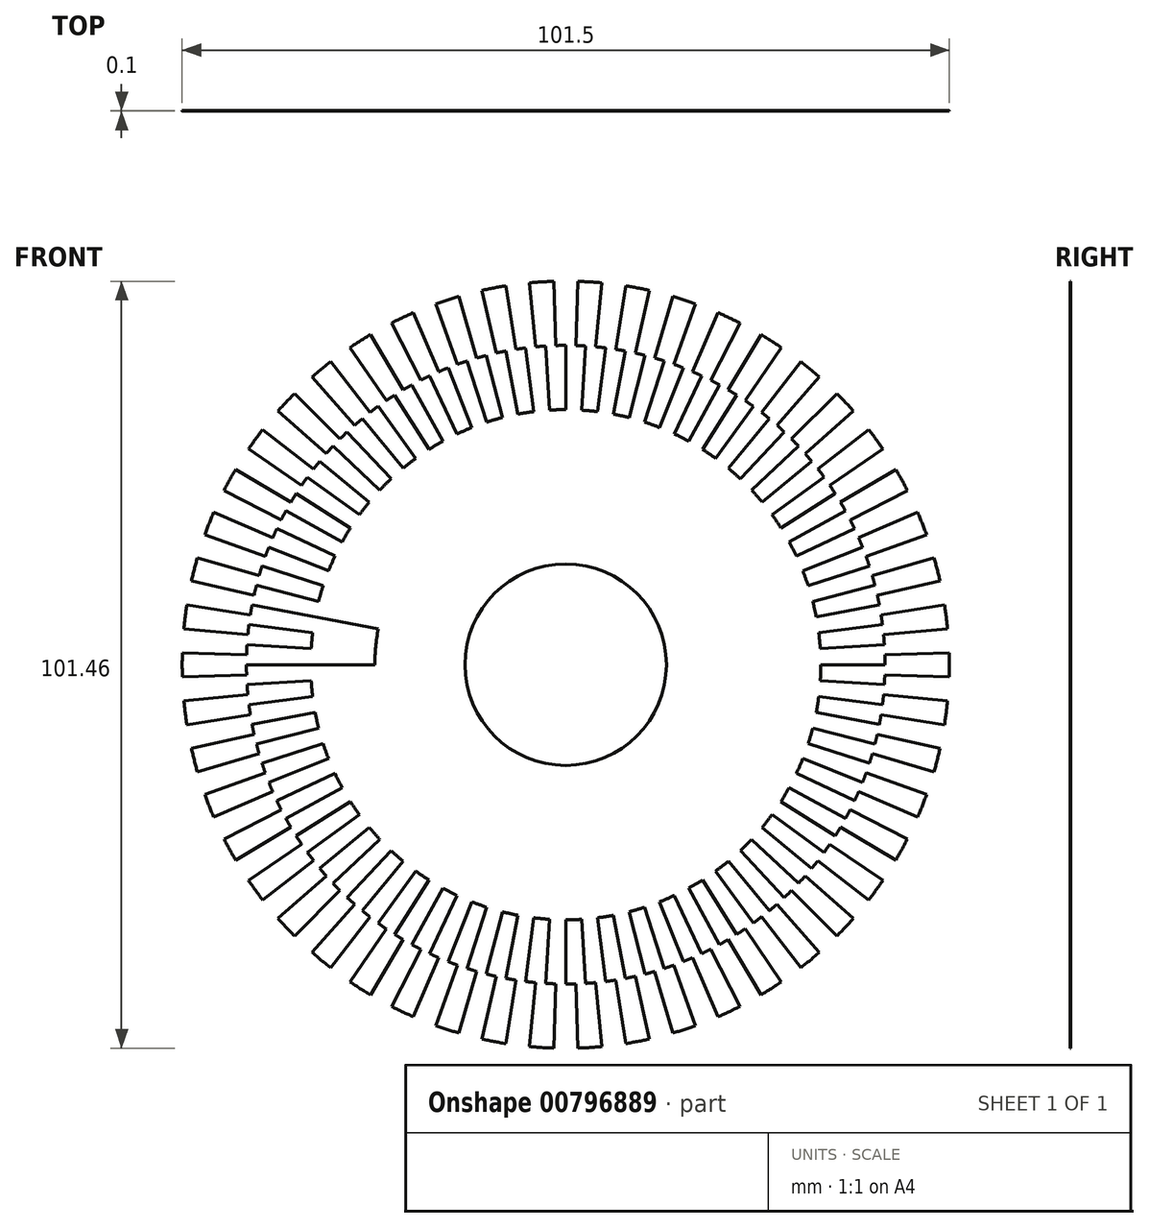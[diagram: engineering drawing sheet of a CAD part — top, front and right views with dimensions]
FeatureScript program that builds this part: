
annotation { "Feature Type Name" : "Feature", "Feature Type Description" : "" }
export const myFeature = defineFeature(function(context is Context, id is Id, definition is map)
    precondition{}
    {
        {
            var Q0;
            Q0=qCreatedBy(makeId("Front.planeOp"),FACE);
            var sketch = newSketch(context, id + "F0", { "sketchPlane" : qUnion([Q0])});
            skCircle(sketch, "E0", {"center": v(0, 0) * mm, "radius": 38 * mm, "construction": true});
            skCircle(sketch, "E1", {"center": v(0, 0) * mm, "radius": 29.5 * mm, "construction": true});
            skCircle(sketch, "E2", {"center": v(0, 0) * mm, "radius": 46.5 * mm, "construction": true});
            skArc(sketch, "E3.0", {"start": v(-33.68, 2.12) * mm, "mid": v(-33.73, 1.06) * mm, "end": v(-33.75, 0) * mm});
            skArc(sketch, "E4.0", {"start": v(-42.17, 2.65) * mm, "mid": v(-42.25, 0.66) * mm, "end": v(-42.23, -1.33) * mm});
            skArc(sketch, "E5.0", {"start": v(-50.73, 1.6) * mm, "mid": v(-50.75, 0) * mm, "end": v(-50.73, -1.6) * mm});
            skLineSegment(sketch, "E6", {"start": v(-25.25, 0) * mm, "end": v(-33.75, 0) * mm});
            skLineSegment(sketch, "E7.trimOffspring", {"start": v(-33.68, 2.12) * mm, "end": v(-42.17, 2.65) * mm});
            skLineSegment(sketch, "E8.trimOffspring", {"start": v(-33.75, 0) * mm, "end": v(-42.25, 0) * mm});
            skLineSegment(sketch, "E9.trimOffspring", {"start": v(-42.23, 1.33) * mm, "end": v(-50.73, 1.6) * mm});
            skLineSegment(sketch, "E10.trimOffspring", {"start": v(-42.23, -1.33) * mm, "end": v(-50.73, -1.6) * mm});
            skLineSegment(sketch, "E11", {"start": v(-24.8, 4.73) * mm, "end": v(-33.15, 6.32) * mm});
            skArc(sketch, "E12", {"start": v(-25.25, 0) * mm, "mid": v(-25.14, 2.38) * mm, "end": v(-24.8, 4.73) * mm});
            skArc(sketch, "E13", {"start": v(-33.75, 0) * mm, "mid": v(-33.6, 3.18) * mm, "end": v(-33.15, 6.32) * mm});
            skLineSegment(sketch, "E14", {"start": v(0, 0) * mm, "end": v(-70.43, 0) * mm, "construction": true});
            skLineSegment(sketch, "E15", {"start": v(0, 0) * mm, "end": v(-33.68, 2.12) * mm, "construction": true});
            skLineSegment(sketch, "E16", {"start": v(0, 0) * mm, "end": v(-42.23, -1.33) * mm, "construction": true});
            skLineSegment(sketch, "E17", {"start": v(0, 0) * mm, "end": v(-42.23, 1.33) * mm, "construction": true});
            skLineSegment(sketch, "E18.1.0", {"start": v(-41.73, -6.6) * mm, "end": v(-50.13, -7.94) * mm});
            skArc(sketch, "E18.1.1", {"start": v(-50.53, -4.78) * mm, "mid": v(-50.35, -6.36) * mm, "end": v(-50.13, -7.94) * mm});
            skLineSegment(sketch, "E18.1.2", {"start": v(-42.06, -3.98) * mm, "end": v(-50.53, -4.78) * mm});
            skArc(sketch, "E18.1.3", {"start": v(-42.17, -2.65) * mm, "mid": v(-42, -4.64) * mm, "end": v(-41.73, -6.6) * mm});
            skLineSegment(sketch, "E18.1.4", {"start": v(-33.68, -2.12) * mm, "end": v(-42.17, -2.65) * mm});
            skArc(sketch, "E18.1.5", {"start": v(-33.68, -2.12) * mm, "mid": v(-33.6, -3.18) * mm, "end": v(-33.48, -4.23) * mm});
            skLineSegment(sketch, "E18.1.6", {"start": v(-33.48, -4.23) * mm, "end": v(-41.92, -5.3) * mm});
            skLineSegment(sketch, "E18.2.0", {"start": v(-40.57, -11.79) * mm, "end": v(-48.74, -14.16) * mm});
            skArc(sketch, "E18.2.1", {"start": v(-49.53, -11.07) * mm, "mid": v(-49.16, -12.62) * mm, "end": v(-48.74, -14.16) * mm});
            skLineSegment(sketch, "E18.2.2", {"start": v(-41.23, -9.22) * mm, "end": v(-49.53, -11.07) * mm});
            skArc(sketch, "E18.2.3", {"start": v(-41.5, -7.92) * mm, "mid": v(-41.08, -9.86) * mm, "end": v(-40.57, -11.79) * mm});
            skLineSegment(sketch, "E18.2.4", {"start": v(-33.15, -6.32) * mm, "end": v(-41.5, -7.92) * mm});
            skArc(sketch, "E18.2.5", {"start": v(-33.15, -6.32) * mm, "mid": v(-32.94, -7.36) * mm, "end": v(-32.7, -8.4) * mm});
            skLineSegment(sketch, "E18.2.6", {"start": v(-32.7, -8.4) * mm, "end": v(-40.92, -10.5) * mm});
            skLineSegment(sketch, "E18.3.0", {"start": v(-38.78, -16.78) * mm, "end": v(-46.58, -20.16) * mm});
            skArc(sketch, "E18.3.1", {"start": v(-47.75, -17.2) * mm, "mid": v(-47.19, -18.68) * mm, "end": v(-46.58, -20.16) * mm});
            skLineSegment(sketch, "E18.3.2", {"start": v(-39.75, -14.31) * mm, "end": v(-47.75, -17.2) * mm});
            skArc(sketch, "E18.3.3", {"start": v(-40.18, -13.06) * mm, "mid": v(-39.52, -14.93) * mm, "end": v(-38.78, -16.78) * mm});
            skLineSegment(sketch, "E18.3.4", {"start": v(-32.1, -10.43) * mm, "end": v(-40.18, -13.06) * mm});
            skArc(sketch, "E18.3.5", {"start": v(-32.1, -10.43) * mm, "mid": v(-31.76, -11.43) * mm, "end": v(-31.38, -12.42) * mm});
            skLineSegment(sketch, "E18.3.6", {"start": v(-31.38, -12.42) * mm, "end": v(-39.28, -15.55) * mm});
            skLineSegment(sketch, "E18.4.0", {"start": v(-36.37, -21.5) * mm, "end": v(-43.68, -25.83) * mm});
            skArc(sketch, "E18.4.1", {"start": v(-45.22, -23.04) * mm, "mid": v(-44.47, -24.45) * mm, "end": v(-43.68, -25.83) * mm});
            skLineSegment(sketch, "E18.4.2", {"start": v(-37.65, -19.18) * mm, "end": v(-45.22, -23.04) * mm});
            skArc(sketch, "E18.4.3", {"start": v(-38.23, -17.99) * mm, "mid": v(-37.34, -19.77) * mm, "end": v(-36.37, -21.5) * mm});
            skLineSegment(sketch, "E18.4.4", {"start": v(-30.54, -14.37) * mm, "end": v(-38.23, -17.99) * mm});
            skArc(sketch, "E18.4.5", {"start": v(-30.54, -14.37) * mm, "mid": v(-30.07, -15.32) * mm, "end": v(-29.58, -16.26) * mm});
            skLineSegment(sketch, "E18.4.6", {"start": v(-29.58, -16.26) * mm, "end": v(-37.02, -20.35) * mm});
            skLineSegment(sketch, "E18.5.0", {"start": v(-33.38, -25.9) * mm, "end": v(-40.1, -31.1) * mm});
            skArc(sketch, "E18.5.1", {"start": v(-41.98, -28.53) * mm, "mid": v(-41.06, -29.83) * mm, "end": v(-40.1, -31.1) * mm});
            skLineSegment(sketch, "E18.5.2", {"start": v(-34.94, -23.75) * mm, "end": v(-41.98, -28.53) * mm});
            skArc(sketch, "E18.5.3", {"start": v(-35.67, -22.64) * mm, "mid": v(-34.57, -24.3) * mm, "end": v(-33.38, -25.9) * mm});
            skLineSegment(sketch, "E18.5.4", {"start": v(-28.5, -18.08) * mm, "end": v(-35.67, -22.64) * mm});
            skArc(sketch, "E18.5.5", {"start": v(-28.5, -18.08) * mm, "mid": v(-27.91, -18.97) * mm, "end": v(-27.3, -19.84) * mm});
            skLineSegment(sketch, "E18.5.6", {"start": v(-27.3, -19.84) * mm, "end": v(-34.18, -24.83) * mm});
            skLineSegment(sketch, "E18.6.0", {"start": v(-29.88, -29.88) * mm, "end": v(-35.89, -35.89) * mm});
            skArc(sketch, "E18.6.1", {"start": v(-38.07, -33.56) * mm, "mid": v(-37, -34.74) * mm, "end": v(-35.89, -35.89) * mm});
            skLineSegment(sketch, "E18.6.2", {"start": v(-31.7, -27.94) * mm, "end": v(-38.07, -33.56) * mm});
            skArc(sketch, "E18.6.3", {"start": v(-32.55, -26.93) * mm, "mid": v(-31.25, -28.44) * mm, "end": v(-29.88, -29.88) * mm});
            skLineSegment(sketch, "E18.6.4", {"start": v(-26, -21.51) * mm, "end": v(-32.55, -26.93) * mm});
            skArc(sketch, "E18.6.5", {"start": v(-26, -21.51) * mm, "mid": v(-25.32, -22.32) * mm, "end": v(-24.6, -23.1) * mm});
            skLineSegment(sketch, "E18.6.6", {"start": v(-24.6, -23.1) * mm, "end": v(-30.8, -28.92) * mm});
            skLineSegment(sketch, "E18.7.0", {"start": v(-25.9, -33.38) * mm, "end": v(-31.1, -40.1) * mm});
            skArc(sketch, "E18.7.1", {"start": v(-33.56, -38.07) * mm, "mid": v(-32.35, -39.1) * mm, "end": v(-31.1, -40.1) * mm});
            skLineSegment(sketch, "E18.7.2", {"start": v(-27.94, -31.7) * mm, "end": v(-33.56, -38.07) * mm});
            skArc(sketch, "E18.7.3", {"start": v(-28.92, -30.8) * mm, "mid": v(-27.44, -32.13) * mm, "end": v(-25.9, -33.38) * mm});
            skLineSegment(sketch, "E18.7.4", {"start": v(-23.1, -24.6) * mm, "end": v(-28.92, -30.8) * mm});
            skArc(sketch, "E18.7.5", {"start": v(-23.1, -24.6) * mm, "mid": v(-22.32, -25.32) * mm, "end": v(-21.51, -26) * mm});
            skLineSegment(sketch, "E18.7.6", {"start": v(-21.51, -26) * mm, "end": v(-26.93, -32.55) * mm});
            skLineSegment(sketch, "E18.8.0", {"start": v(-21.5, -36.37) * mm, "end": v(-25.83, -43.68) * mm});
            skArc(sketch, "E18.8.1", {"start": v(-28.53, -41.98) * mm, "mid": v(-27.2, -42.85) * mm, "end": v(-25.83, -43.68) * mm});
            skLineSegment(sketch, "E18.8.2", {"start": v(-23.75, -34.94) * mm, "end": v(-28.53, -41.98) * mm});
            skArc(sketch, "E18.8.3", {"start": v(-24.83, -34.18) * mm, "mid": v(-23.2, -35.31) * mm, "end": v(-21.5, -36.37) * mm});
            skLineSegment(sketch, "E18.8.4", {"start": v(-19.84, -27.3) * mm, "end": v(-24.83, -34.18) * mm});
            skArc(sketch, "E18.8.5", {"start": v(-19.84, -27.3) * mm, "mid": v(-18.97, -27.91) * mm, "end": v(-18.08, -28.5) * mm});
            skLineSegment(sketch, "E18.8.6", {"start": v(-18.08, -28.5) * mm, "end": v(-22.64, -35.67) * mm});
            skLineSegment(sketch, "E18.9.0", {"start": v(-16.78, -38.78) * mm, "end": v(-20.16, -46.58) * mm});
            skArc(sketch, "E18.9.1", {"start": v(-23.04, -45.22) * mm, "mid": v(-21.6, -45.92) * mm, "end": v(-20.16, -46.58) * mm});
            skLineSegment(sketch, "E18.9.2", {"start": v(-19.18, -37.65) * mm, "end": v(-23.04, -45.22) * mm});
            skArc(sketch, "E18.9.3", {"start": v(-20.35, -37.02) * mm, "mid": v(-18.59, -37.94) * mm, "end": v(-16.78, -38.78) * mm});
            skLineSegment(sketch, "E18.9.4", {"start": v(-16.26, -29.58) * mm, "end": v(-20.35, -37.02) * mm});
            skArc(sketch, "E18.9.5", {"start": v(-16.26, -29.58) * mm, "mid": v(-15.32, -30.07) * mm, "end": v(-14.37, -30.54) * mm});
            skLineSegment(sketch, "E18.9.6", {"start": v(-14.37, -30.54) * mm, "end": v(-17.99, -38.23) * mm});
            skLineSegment(sketch, "E18.10.0", {"start": v(-11.79, -40.57) * mm, "end": v(-14.16, -48.74) * mm});
            skArc(sketch, "E18.10.1", {"start": v(-17.2, -47.75) * mm, "mid": v(-15.68, -48.27) * mm, "end": v(-14.16, -48.74) * mm});
            skLineSegment(sketch, "E18.10.2", {"start": v(-14.31, -39.75) * mm, "end": v(-17.2, -47.75) * mm});
            skArc(sketch, "E18.10.3", {"start": v(-15.55, -39.28) * mm, "mid": v(-13.69, -39.97) * mm, "end": v(-11.79, -40.57) * mm});
            skLineSegment(sketch, "E18.10.4", {"start": v(-12.42, -31.38) * mm, "end": v(-15.55, -39.28) * mm});
            skArc(sketch, "E18.10.5", {"start": v(-12.42, -31.38) * mm, "mid": v(-11.43, -31.76) * mm, "end": v(-10.43, -32.1) * mm});
            skLineSegment(sketch, "E18.10.6", {"start": v(-10.43, -32.1) * mm, "end": v(-13.06, -40.18) * mm});
            skLineSegment(sketch, "E18.11.0", {"start": v(-6.6, -41.73) * mm, "end": v(-7.94, -50.13) * mm});
            skArc(sketch, "E18.11.1", {"start": v(-11.07, -49.53) * mm, "mid": v(-9.5, -49.85) * mm, "end": v(-7.94, -50.13) * mm});
            skLineSegment(sketch, "E18.11.2", {"start": v(-9.22, -41.23) * mm, "end": v(-11.07, -49.53) * mm});
            skArc(sketch, "E18.11.3", {"start": v(-10.5, -40.92) * mm, "mid": v(-8.57, -41.37) * mm, "end": v(-6.6, -41.73) * mm});
            skLineSegment(sketch, "E18.11.4", {"start": v(-8.4, -32.7) * mm, "end": v(-10.5, -40.92) * mm});
            skArc(sketch, "E18.11.5", {"start": v(-8.4, -32.7) * mm, "mid": v(-7.36, -32.94) * mm, "end": v(-6.32, -33.15) * mm});
            skLineSegment(sketch, "E18.11.6", {"start": v(-6.32, -33.15) * mm, "end": v(-7.92, -41.5) * mm});
            skLineSegment(sketch, "E18.12.0", {"start": v(-1.33, -42.23) * mm, "end": v(-1.6, -50.73) * mm});
            skArc(sketch, "E18.12.1", {"start": v(-4.78, -50.53) * mm, "mid": v(-3.19, -50.65) * mm, "end": v(-1.6, -50.73) * mm});
            skLineSegment(sketch, "E18.12.2", {"start": v(-3.98, -42.06) * mm, "end": v(-4.78, -50.53) * mm});
            skArc(sketch, "E18.12.3", {"start": v(-5.3, -41.92) * mm, "mid": v(-3.31, -42.12) * mm, "end": v(-1.33, -42.23) * mm});
            skLineSegment(sketch, "E18.12.4", {"start": v(-4.23, -33.48) * mm, "end": v(-5.3, -41.92) * mm});
            skArc(sketch, "E18.12.5", {"start": v(-4.23, -33.48) * mm, "mid": v(-3.18, -33.6) * mm, "end": v(-2.12, -33.68) * mm});
            skLineSegment(sketch, "E18.12.6", {"start": v(-2.12, -33.68) * mm, "end": v(-2.65, -42.17) * mm});
            skLineSegment(sketch, "E18.13.0", {"start": v(3.98, -42.06) * mm, "end": v(4.78, -50.53) * mm});
            skArc(sketch, "E18.13.1", {"start": v(1.6, -50.73) * mm, "mid": v(3.19, -50.65) * mm, "end": v(4.78, -50.53) * mm});
            skLineSegment(sketch, "E18.13.2", {"start": v(1.33, -42.23) * mm, "end": v(1.6, -50.73) * mm});
            skArc(sketch, "E18.13.3", {"start": v(0, -42.25) * mm, "mid": v(2, -42.2) * mm, "end": v(3.98, -42.06) * mm});
            skLineSegment(sketch, "E18.13.4", {"start": v(0, -33.75) * mm, "end": v(0, -42.25) * mm});
            skArc(sketch, "E18.13.5", {"start": v(0, -33.75) * mm, "mid": v(1.06, -33.73) * mm, "end": v(2.12, -33.68) * mm});
            skLineSegment(sketch, "E18.13.6", {"start": v(2.12, -33.68) * mm, "end": v(2.65, -42.17) * mm});
            skLineSegment(sketch, "E18.14.0", {"start": v(9.22, -41.23) * mm, "end": v(11.07, -49.53) * mm});
            skArc(sketch, "E18.14.1", {"start": v(7.94, -50.13) * mm, "mid": v(9.5, -49.85) * mm, "end": v(11.07, -49.53) * mm});
            skLineSegment(sketch, "E18.14.2", {"start": v(6.6, -41.73) * mm, "end": v(7.94, -50.13) * mm});
            skArc(sketch, "E18.14.3", {"start": v(5.3, -41.92) * mm, "mid": v(7.26, -41.62) * mm, "end": v(9.22, -41.23) * mm});
            skLineSegment(sketch, "E18.14.4", {"start": v(4.23, -33.48) * mm, "end": v(5.3, -41.92) * mm});
            skArc(sketch, "E18.14.5", {"start": v(4.23, -33.48) * mm, "mid": v(5.28, -33.34) * mm, "end": v(6.32, -33.15) * mm});
            skLineSegment(sketch, "E18.14.6", {"start": v(6.32, -33.15) * mm, "end": v(7.92, -41.5) * mm});
            skLineSegment(sketch, "E18.15.0", {"start": v(14.31, -39.75) * mm, "end": v(17.2, -47.75) * mm});
            skArc(sketch, "E18.15.1", {"start": v(14.16, -48.74) * mm, "mid": v(15.68, -48.27) * mm, "end": v(17.2, -47.75) * mm});
            skLineSegment(sketch, "E18.15.2", {"start": v(11.79, -40.57) * mm, "end": v(14.16, -48.74) * mm});
            skArc(sketch, "E18.15.3", {"start": v(10.5, -40.92) * mm, "mid": v(12.42, -40.38) * mm, "end": v(14.31, -39.75) * mm});
            skLineSegment(sketch, "E18.15.4", {"start": v(8.4, -32.7) * mm, "end": v(10.5, -40.92) * mm});
            skArc(sketch, "E18.15.5", {"start": v(8.4, -32.7) * mm, "mid": v(9.42, -32.41) * mm, "end": v(10.43, -32.1) * mm});
            skLineSegment(sketch, "E18.15.6", {"start": v(10.43, -32.1) * mm, "end": v(13.06, -40.18) * mm});
            skLineSegment(sketch, "E18.16.0", {"start": v(19.18, -37.65) * mm, "end": v(23.04, -45.22) * mm});
            skArc(sketch, "E18.16.1", {"start": v(20.16, -46.58) * mm, "mid": v(21.6, -45.92) * mm, "end": v(23.04, -45.22) * mm});
            skLineSegment(sketch, "E18.16.2", {"start": v(16.78, -38.78) * mm, "end": v(20.16, -46.58) * mm});
            skArc(sketch, "E18.16.3", {"start": v(15.55, -39.28) * mm, "mid": v(17.39, -38.5) * mm, "end": v(19.18, -37.65) * mm});
            skLineSegment(sketch, "E18.16.4", {"start": v(12.42, -31.38) * mm, "end": v(15.55, -39.28) * mm});
            skArc(sketch, "E18.16.5", {"start": v(12.42, -31.38) * mm, "mid": v(13.4, -30.98) * mm, "end": v(14.37, -30.54) * mm});
            skLineSegment(sketch, "E18.16.6", {"start": v(14.37, -30.54) * mm, "end": v(17.99, -38.23) * mm});
            skLineSegment(sketch, "E18.17.0", {"start": v(23.75, -34.94) * mm, "end": v(28.53, -41.98) * mm});
            skArc(sketch, "E18.17.1", {"start": v(25.83, -43.68) * mm, "mid": v(27.2, -42.85) * mm, "end": v(28.53, -41.98) * mm});
            skLineSegment(sketch, "E18.17.2", {"start": v(21.5, -36.37) * mm, "end": v(25.83, -43.68) * mm});
            skArc(sketch, "E18.17.3", {"start": v(20.35, -37.02) * mm, "mid": v(22.08, -36.02) * mm, "end": v(23.75, -34.94) * mm});
            skLineSegment(sketch, "E18.17.4", {"start": v(16.26, -29.58) * mm, "end": v(20.35, -37.02) * mm});
            skArc(sketch, "E18.17.5", {"start": v(16.26, -29.58) * mm, "mid": v(17.18, -29.05) * mm, "end": v(18.08, -28.5) * mm});
            skLineSegment(sketch, "E18.17.6", {"start": v(18.08, -28.5) * mm, "end": v(22.64, -35.67) * mm});
            skLineSegment(sketch, "E18.18.0", {"start": v(27.94, -31.7) * mm, "end": v(33.56, -38.07) * mm});
            skArc(sketch, "E18.18.1", {"start": v(31.1, -40.1) * mm, "mid": v(32.35, -39.1) * mm, "end": v(33.56, -38.07) * mm});
            skLineSegment(sketch, "E18.18.2", {"start": v(25.9, -33.38) * mm, "end": v(31.1, -40.1) * mm});
            skArc(sketch, "E18.18.3", {"start": v(24.83, -34.18) * mm, "mid": v(26.42, -32.97) * mm, "end": v(27.94, -31.7) * mm});
            skLineSegment(sketch, "E18.18.4", {"start": v(19.84, -27.3) * mm, "end": v(24.83, -34.18) * mm});
            skArc(sketch, "E18.18.5", {"start": v(19.84, -27.3) * mm, "mid": v(20.69, -26.67) * mm, "end": v(21.51, -26) * mm});
            skLineSegment(sketch, "E18.18.6", {"start": v(21.51, -26) * mm, "end": v(26.93, -32.55) * mm});
            skLineSegment(sketch, "E18.19.0", {"start": v(31.7, -27.94) * mm, "end": v(38.07, -33.56) * mm});
            skArc(sketch, "E18.19.1", {"start": v(35.89, -35.89) * mm, "mid": v(37, -34.74) * mm, "end": v(38.07, -33.56) * mm});
            skLineSegment(sketch, "E18.19.2", {"start": v(29.88, -29.88) * mm, "end": v(35.89, -35.89) * mm});
            skArc(sketch, "E18.19.3", {"start": v(28.92, -30.8) * mm, "mid": v(30.34, -29.4) * mm, "end": v(31.7, -27.94) * mm});
            skLineSegment(sketch, "E18.19.4", {"start": v(23.1, -24.6) * mm, "end": v(28.92, -30.8) * mm});
            skArc(sketch, "E18.19.5", {"start": v(23.1, -24.6) * mm, "mid": v(23.87, -23.87) * mm, "end": v(24.6, -23.1) * mm});
            skLineSegment(sketch, "E18.19.6", {"start": v(24.6, -23.1) * mm, "end": v(30.8, -28.92) * mm});
            skLineSegment(sketch, "E18.20.0", {"start": v(34.94, -23.75) * mm, "end": v(41.98, -28.53) * mm});
            skArc(sketch, "E18.20.1", {"start": v(40.1, -31.1) * mm, "mid": v(41.06, -29.83) * mm, "end": v(41.98, -28.53) * mm});
            skLineSegment(sketch, "E18.20.2", {"start": v(33.38, -25.9) * mm, "end": v(40.1, -31.1) * mm});
            skArc(sketch, "E18.20.3", {"start": v(32.55, -26.93) * mm, "mid": v(33.79, -25.37) * mm, "end": v(34.94, -23.75) * mm});
            skLineSegment(sketch, "E18.20.4", {"start": v(26, -21.51) * mm, "end": v(32.55, -26.93) * mm});
            skArc(sketch, "E18.20.5", {"start": v(26, -21.51) * mm, "mid": v(26.67, -20.69) * mm, "end": v(27.3, -19.84) * mm});
            skLineSegment(sketch, "E18.20.6", {"start": v(27.3, -19.84) * mm, "end": v(34.18, -24.83) * mm});
            skLineSegment(sketch, "E18.21.0", {"start": v(37.65, -19.18) * mm, "end": v(45.22, -23.04) * mm});
            skArc(sketch, "E18.21.1", {"start": v(43.68, -25.83) * mm, "mid": v(44.47, -24.45) * mm, "end": v(45.22, -23.04) * mm});
            skLineSegment(sketch, "E18.21.2", {"start": v(36.37, -21.5) * mm, "end": v(43.68, -25.83) * mm});
            skArc(sketch, "E18.21.3", {"start": v(35.67, -22.64) * mm, "mid": v(36.7, -20.93) * mm, "end": v(37.65, -19.18) * mm});
            skLineSegment(sketch, "E18.21.4", {"start": v(28.5, -18.08) * mm, "end": v(35.67, -22.64) * mm});
            skArc(sketch, "E18.21.5", {"start": v(28.5, -18.08) * mm, "mid": v(29.05, -17.18) * mm, "end": v(29.58, -16.26) * mm});
            skLineSegment(sketch, "E18.21.6", {"start": v(29.58, -16.26) * mm, "end": v(37.02, -20.35) * mm});
            skLineSegment(sketch, "E18.22.0", {"start": v(39.75, -14.31) * mm, "end": v(47.75, -17.2) * mm});
            skArc(sketch, "E18.22.1", {"start": v(46.58, -20.16) * mm, "mid": v(47.19, -18.68) * mm, "end": v(47.75, -17.2) * mm});
            skLineSegment(sketch, "E18.22.2", {"start": v(38.78, -16.78) * mm, "end": v(46.58, -20.16) * mm});
            skArc(sketch, "E18.22.3", {"start": v(38.23, -17.99) * mm, "mid": v(39.03, -16.17) * mm, "end": v(39.75, -14.31) * mm});
            skLineSegment(sketch, "E18.22.4", {"start": v(30.54, -14.37) * mm, "end": v(38.23, -17.99) * mm});
            skArc(sketch, "E18.22.5", {"start": v(30.54, -14.37) * mm, "mid": v(30.98, -13.4) * mm, "end": v(31.38, -12.42) * mm});
            skLineSegment(sketch, "E18.22.6", {"start": v(31.38, -12.42) * mm, "end": v(39.28, -15.55) * mm});
            skLineSegment(sketch, "E18.23.0", {"start": v(41.23, -9.22) * mm, "end": v(49.53, -11.07) * mm});
            skArc(sketch, "E18.23.1", {"start": v(48.74, -14.16) * mm, "mid": v(49.16, -12.62) * mm, "end": v(49.53, -11.07) * mm});
            skLineSegment(sketch, "E18.23.2", {"start": v(40.57, -11.79) * mm, "end": v(48.74, -14.16) * mm});
            skArc(sketch, "E18.23.3", {"start": v(40.18, -13.06) * mm, "mid": v(40.75, -11.15) * mm, "end": v(41.23, -9.22) * mm});
            skLineSegment(sketch, "E18.23.4", {"start": v(32.1, -10.43) * mm, "end": v(40.18, -13.06) * mm});
            skArc(sketch, "E18.23.5", {"start": v(32.1, -10.43) * mm, "mid": v(32.41, -9.42) * mm, "end": v(32.7, -8.4) * mm});
            skLineSegment(sketch, "E18.23.6", {"start": v(32.7, -8.4) * mm, "end": v(40.92, -10.5) * mm});
            skLineSegment(sketch, "E18.24.0", {"start": v(42.06, -3.98) * mm, "end": v(50.53, -4.78) * mm});
            skArc(sketch, "E18.24.1", {"start": v(50.13, -7.94) * mm, "mid": v(50.35, -6.36) * mm, "end": v(50.53, -4.78) * mm});
            skLineSegment(sketch, "E18.24.2", {"start": v(41.73, -6.6) * mm, "end": v(50.13, -7.94) * mm});
            skArc(sketch, "E18.24.3", {"start": v(41.5, -7.92) * mm, "mid": v(41.83, -5.95) * mm, "end": v(42.06, -3.98) * mm});
            skLineSegment(sketch, "E18.24.4", {"start": v(33.15, -6.32) * mm, "end": v(41.5, -7.92) * mm});
            skArc(sketch, "E18.24.5", {"start": v(33.15, -6.32) * mm, "mid": v(33.34, -5.28) * mm, "end": v(33.48, -4.23) * mm});
            skLineSegment(sketch, "E18.24.6", {"start": v(33.48, -4.23) * mm, "end": v(41.92, -5.3) * mm});
            skLineSegment(sketch, "E18.25.0", {"start": v(42.23, 1.33) * mm, "end": v(50.73, 1.6) * mm});
            skArc(sketch, "E18.25.1", {"start": v(50.73, -1.6) * mm, "mid": v(50.75, 0) * mm, "end": v(50.73, 1.6) * mm});
            skLineSegment(sketch, "E18.25.2", {"start": v(42.23, -1.33) * mm, "end": v(50.73, -1.6) * mm});
            skArc(sketch, "E18.25.3", {"start": v(42.17, -2.65) * mm, "mid": v(42.25, -0.66) * mm, "end": v(42.23, 1.33) * mm});
            skLineSegment(sketch, "E18.25.4", {"start": v(33.68, -2.12) * mm, "end": v(42.17, -2.65) * mm});
            skArc(sketch, "E18.25.5", {"start": v(33.68, -2.12) * mm, "mid": v(33.73, -1.06) * mm, "end": v(33.75, 0) * mm});
            skLineSegment(sketch, "E18.25.6", {"start": v(33.75, 0) * mm, "end": v(42.25, 0) * mm});
            skLineSegment(sketch, "E18.26.0", {"start": v(41.73, 6.6) * mm, "end": v(50.13, 7.94) * mm});
            skArc(sketch, "E18.26.1", {"start": v(50.53, 4.78) * mm, "mid": v(50.35, 6.36) * mm, "end": v(50.13, 7.94) * mm});
            skLineSegment(sketch, "E18.26.2", {"start": v(42.06, 3.98) * mm, "end": v(50.53, 4.78) * mm});
            skArc(sketch, "E18.26.3", {"start": v(42.17, 2.65) * mm, "mid": v(42, 4.64) * mm, "end": v(41.73, 6.6) * mm});
            skLineSegment(sketch, "E18.26.4", {"start": v(33.68, 2.12) * mm, "end": v(42.17, 2.65) * mm});
            skArc(sketch, "E18.26.5", {"start": v(33.68, 2.12) * mm, "mid": v(33.6, 3.18) * mm, "end": v(33.48, 4.23) * mm});
            skLineSegment(sketch, "E18.26.6", {"start": v(33.48, 4.23) * mm, "end": v(41.92, 5.3) * mm});
            skLineSegment(sketch, "E18.27.0", {"start": v(40.57, 11.79) * mm, "end": v(48.74, 14.16) * mm});
            skArc(sketch, "E18.27.1", {"start": v(49.53, 11.07) * mm, "mid": v(49.16, 12.62) * mm, "end": v(48.74, 14.16) * mm});
            skLineSegment(sketch, "E18.27.2", {"start": v(41.23, 9.22) * mm, "end": v(49.53, 11.07) * mm});
            skArc(sketch, "E18.27.3", {"start": v(41.5, 7.92) * mm, "mid": v(41.08, 9.86) * mm, "end": v(40.57, 11.79) * mm});
            skLineSegment(sketch, "E18.27.4", {"start": v(33.15, 6.32) * mm, "end": v(41.5, 7.92) * mm});
            skArc(sketch, "E18.27.5", {"start": v(33.15, 6.32) * mm, "mid": v(32.94, 7.36) * mm, "end": v(32.7, 8.4) * mm});
            skLineSegment(sketch, "E18.27.6", {"start": v(32.7, 8.4) * mm, "end": v(40.92, 10.5) * mm});
            skLineSegment(sketch, "E18.28.0", {"start": v(38.78, 16.78) * mm, "end": v(46.58, 20.16) * mm});
            skArc(sketch, "E18.28.1", {"start": v(47.75, 17.2) * mm, "mid": v(47.19, 18.68) * mm, "end": v(46.58, 20.16) * mm});
            skLineSegment(sketch, "E18.28.2", {"start": v(39.75, 14.31) * mm, "end": v(47.75, 17.2) * mm});
            skArc(sketch, "E18.28.3", {"start": v(40.18, 13.06) * mm, "mid": v(39.52, 14.93) * mm, "end": v(38.78, 16.78) * mm});
            skLineSegment(sketch, "E18.28.4", {"start": v(32.1, 10.43) * mm, "end": v(40.18, 13.06) * mm});
            skArc(sketch, "E18.28.5", {"start": v(32.1, 10.43) * mm, "mid": v(31.76, 11.43) * mm, "end": v(31.38, 12.42) * mm});
            skLineSegment(sketch, "E18.28.6", {"start": v(31.38, 12.42) * mm, "end": v(39.28, 15.55) * mm});
            skLineSegment(sketch, "E18.29.0", {"start": v(36.37, 21.5) * mm, "end": v(43.68, 25.83) * mm});
            skArc(sketch, "E18.29.1", {"start": v(45.22, 23.04) * mm, "mid": v(44.47, 24.45) * mm, "end": v(43.68, 25.83) * mm});
            skLineSegment(sketch, "E18.29.2", {"start": v(37.65, 19.18) * mm, "end": v(45.22, 23.04) * mm});
            skArc(sketch, "E18.29.3", {"start": v(38.23, 17.99) * mm, "mid": v(37.34, 19.77) * mm, "end": v(36.37, 21.5) * mm});
            skLineSegment(sketch, "E18.29.4", {"start": v(30.54, 14.37) * mm, "end": v(38.23, 17.99) * mm});
            skArc(sketch, "E18.29.5", {"start": v(30.54, 14.37) * mm, "mid": v(30.07, 15.32) * mm, "end": v(29.58, 16.26) * mm});
            skLineSegment(sketch, "E18.29.6", {"start": v(29.58, 16.26) * mm, "end": v(37.02, 20.35) * mm});
            skLineSegment(sketch, "E18.30.0", {"start": v(33.38, 25.9) * mm, "end": v(40.1, 31.1) * mm});
            skArc(sketch, "E18.30.1", {"start": v(41.98, 28.53) * mm, "mid": v(41.06, 29.83) * mm, "end": v(40.1, 31.1) * mm});
            skLineSegment(sketch, "E18.30.2", {"start": v(34.94, 23.75) * mm, "end": v(41.98, 28.53) * mm});
            skArc(sketch, "E18.30.3", {"start": v(35.67, 22.64) * mm, "mid": v(34.57, 24.3) * mm, "end": v(33.38, 25.9) * mm});
            skLineSegment(sketch, "E18.30.4", {"start": v(28.5, 18.08) * mm, "end": v(35.67, 22.64) * mm});
            skArc(sketch, "E18.30.5", {"start": v(28.5, 18.08) * mm, "mid": v(27.91, 18.97) * mm, "end": v(27.3, 19.84) * mm});
            skLineSegment(sketch, "E18.30.6", {"start": v(27.3, 19.84) * mm, "end": v(34.18, 24.83) * mm});
            skLineSegment(sketch, "E18.31.0", {"start": v(29.88, 29.88) * mm, "end": v(35.89, 35.89) * mm});
            skArc(sketch, "E18.31.1", {"start": v(38.07, 33.56) * mm, "mid": v(37, 34.74) * mm, "end": v(35.89, 35.89) * mm});
            skLineSegment(sketch, "E18.31.2", {"start": v(31.7, 27.94) * mm, "end": v(38.07, 33.56) * mm});
            skArc(sketch, "E18.31.3", {"start": v(32.55, 26.93) * mm, "mid": v(31.25, 28.44) * mm, "end": v(29.88, 29.88) * mm});
            skLineSegment(sketch, "E18.31.4", {"start": v(26, 21.51) * mm, "end": v(32.55, 26.93) * mm});
            skArc(sketch, "E18.31.5", {"start": v(26, 21.51) * mm, "mid": v(25.32, 22.32) * mm, "end": v(24.6, 23.1) * mm});
            skLineSegment(sketch, "E18.31.6", {"start": v(24.6, 23.1) * mm, "end": v(30.8, 28.92) * mm});
            skLineSegment(sketch, "E18.32.0", {"start": v(25.9, 33.38) * mm, "end": v(31.1, 40.1) * mm});
            skArc(sketch, "E18.32.1", {"start": v(33.56, 38.07) * mm, "mid": v(32.35, 39.1) * mm, "end": v(31.1, 40.1) * mm});
            skLineSegment(sketch, "E18.32.2", {"start": v(27.94, 31.7) * mm, "end": v(33.56, 38.07) * mm});
            skArc(sketch, "E18.32.3", {"start": v(28.92, 30.8) * mm, "mid": v(27.44, 32.13) * mm, "end": v(25.9, 33.38) * mm});
            skLineSegment(sketch, "E18.32.4", {"start": v(23.1, 24.6) * mm, "end": v(28.92, 30.8) * mm});
            skArc(sketch, "E18.32.5", {"start": v(23.1, 24.6) * mm, "mid": v(22.32, 25.32) * mm, "end": v(21.51, 26) * mm});
            skLineSegment(sketch, "E18.32.6", {"start": v(21.51, 26) * mm, "end": v(26.93, 32.55) * mm});
            skLineSegment(sketch, "E18.33.0", {"start": v(21.5, 36.37) * mm, "end": v(25.83, 43.68) * mm});
            skArc(sketch, "E18.33.1", {"start": v(28.53, 41.98) * mm, "mid": v(27.2, 42.85) * mm, "end": v(25.83, 43.68) * mm});
            skLineSegment(sketch, "E18.33.2", {"start": v(23.75, 34.94) * mm, "end": v(28.53, 41.98) * mm});
            skArc(sketch, "E18.33.3", {"start": v(24.83, 34.18) * mm, "mid": v(23.2, 35.31) * mm, "end": v(21.5, 36.37) * mm});
            skLineSegment(sketch, "E18.33.4", {"start": v(19.84, 27.3) * mm, "end": v(24.83, 34.18) * mm});
            skArc(sketch, "E18.33.5", {"start": v(19.84, 27.3) * mm, "mid": v(18.97, 27.91) * mm, "end": v(18.08, 28.5) * mm});
            skLineSegment(sketch, "E18.33.6", {"start": v(18.08, 28.5) * mm, "end": v(22.64, 35.67) * mm});
            skLineSegment(sketch, "E18.34.0", {"start": v(16.78, 38.78) * mm, "end": v(20.16, 46.58) * mm});
            skArc(sketch, "E18.34.1", {"start": v(23.04, 45.22) * mm, "mid": v(21.6, 45.92) * mm, "end": v(20.16, 46.58) * mm});
            skLineSegment(sketch, "E18.34.2", {"start": v(19.18, 37.65) * mm, "end": v(23.04, 45.22) * mm});
            skArc(sketch, "E18.34.3", {"start": v(20.35, 37.02) * mm, "mid": v(18.59, 37.94) * mm, "end": v(16.78, 38.78) * mm});
            skLineSegment(sketch, "E18.34.4", {"start": v(16.26, 29.58) * mm, "end": v(20.35, 37.02) * mm});
            skArc(sketch, "E18.34.5", {"start": v(16.26, 29.58) * mm, "mid": v(15.32, 30.07) * mm, "end": v(14.37, 30.54) * mm});
            skLineSegment(sketch, "E18.34.6", {"start": v(14.37, 30.54) * mm, "end": v(17.99, 38.23) * mm});
            skLineSegment(sketch, "E18.35.0", {"start": v(11.79, 40.57) * mm, "end": v(14.16, 48.74) * mm});
            skArc(sketch, "E18.35.1", {"start": v(17.2, 47.75) * mm, "mid": v(15.68, 48.27) * mm, "end": v(14.16, 48.74) * mm});
            skLineSegment(sketch, "E18.35.2", {"start": v(14.31, 39.75) * mm, "end": v(17.2, 47.75) * mm});
            skArc(sketch, "E18.35.3", {"start": v(15.55, 39.28) * mm, "mid": v(13.69, 39.97) * mm, "end": v(11.79, 40.57) * mm});
            skLineSegment(sketch, "E18.35.4", {"start": v(12.42, 31.38) * mm, "end": v(15.55, 39.28) * mm});
            skArc(sketch, "E18.35.5", {"start": v(12.42, 31.38) * mm, "mid": v(11.43, 31.76) * mm, "end": v(10.43, 32.1) * mm});
            skLineSegment(sketch, "E18.35.6", {"start": v(10.43, 32.1) * mm, "end": v(13.06, 40.18) * mm});
            skLineSegment(sketch, "E18.36.0", {"start": v(6.6, 41.73) * mm, "end": v(7.94, 50.13) * mm});
            skArc(sketch, "E18.36.1", {"start": v(11.07, 49.53) * mm, "mid": v(9.5, 49.85) * mm, "end": v(7.94, 50.13) * mm});
            skLineSegment(sketch, "E18.36.2", {"start": v(9.22, 41.23) * mm, "end": v(11.07, 49.53) * mm});
            skArc(sketch, "E18.36.3", {"start": v(10.5, 40.92) * mm, "mid": v(8.57, 41.37) * mm, "end": v(6.6, 41.73) * mm});
            skLineSegment(sketch, "E18.36.4", {"start": v(8.4, 32.7) * mm, "end": v(10.5, 40.92) * mm});
            skArc(sketch, "E18.36.5", {"start": v(8.4, 32.7) * mm, "mid": v(7.36, 32.94) * mm, "end": v(6.32, 33.15) * mm});
            skLineSegment(sketch, "E18.36.6", {"start": v(6.32, 33.15) * mm, "end": v(7.92, 41.5) * mm});
            skLineSegment(sketch, "E18.37.0", {"start": v(1.33, 42.23) * mm, "end": v(1.6, 50.73) * mm});
            skArc(sketch, "E18.37.1", {"start": v(4.78, 50.53) * mm, "mid": v(3.19, 50.65) * mm, "end": v(1.6, 50.73) * mm});
            skLineSegment(sketch, "E18.37.2", {"start": v(3.98, 42.06) * mm, "end": v(4.78, 50.53) * mm});
            skArc(sketch, "E18.37.3", {"start": v(5.3, 41.92) * mm, "mid": v(3.31, 42.12) * mm, "end": v(1.33, 42.23) * mm});
            skLineSegment(sketch, "E18.37.4", {"start": v(4.23, 33.48) * mm, "end": v(5.3, 41.92) * mm});
            skArc(sketch, "E18.37.5", {"start": v(4.23, 33.48) * mm, "mid": v(3.18, 33.6) * mm, "end": v(2.12, 33.68) * mm});
            skLineSegment(sketch, "E18.37.6", {"start": v(2.12, 33.68) * mm, "end": v(2.65, 42.17) * mm});
            skLineSegment(sketch, "E18.38.0", {"start": v(-3.98, 42.06) * mm, "end": v(-4.78, 50.53) * mm});
            skArc(sketch, "E18.38.1", {"start": v(-1.6, 50.73) * mm, "mid": v(-3.19, 50.65) * mm, "end": v(-4.78, 50.53) * mm});
            skLineSegment(sketch, "E18.38.2", {"start": v(-1.33, 42.23) * mm, "end": v(-1.6, 50.73) * mm});
            skArc(sketch, "E18.38.3", {"start": v(0, 42.25) * mm, "mid": v(-2, 42.2) * mm, "end": v(-3.98, 42.06) * mm});
            skLineSegment(sketch, "E18.38.4", {"start": v(0, 33.75) * mm, "end": v(0, 42.25) * mm});
            skArc(sketch, "E18.38.5", {"start": v(0, 33.75) * mm, "mid": v(-1.06, 33.73) * mm, "end": v(-2.12, 33.68) * mm});
            skLineSegment(sketch, "E18.38.6", {"start": v(-2.12, 33.68) * mm, "end": v(-2.65, 42.17) * mm});
            skLineSegment(sketch, "E18.39.0", {"start": v(-9.22, 41.23) * mm, "end": v(-11.07, 49.53) * mm});
            skArc(sketch, "E18.39.1", {"start": v(-7.94, 50.13) * mm, "mid": v(-9.5, 49.85) * mm, "end": v(-11.07, 49.53) * mm});
            skLineSegment(sketch, "E18.39.2", {"start": v(-6.6, 41.73) * mm, "end": v(-7.94, 50.13) * mm});
            skArc(sketch, "E18.39.3", {"start": v(-5.3, 41.92) * mm, "mid": v(-7.26, 41.62) * mm, "end": v(-9.22, 41.23) * mm});
            skLineSegment(sketch, "E18.39.4", {"start": v(-4.23, 33.48) * mm, "end": v(-5.3, 41.92) * mm});
            skArc(sketch, "E18.39.5", {"start": v(-4.23, 33.48) * mm, "mid": v(-5.28, 33.34) * mm, "end": v(-6.32, 33.15) * mm});
            skLineSegment(sketch, "E18.39.6", {"start": v(-6.32, 33.15) * mm, "end": v(-7.92, 41.5) * mm});
            skLineSegment(sketch, "E18.40.0", {"start": v(-14.31, 39.75) * mm, "end": v(-17.2, 47.75) * mm});
            skArc(sketch, "E18.40.1", {"start": v(-14.16, 48.74) * mm, "mid": v(-15.68, 48.27) * mm, "end": v(-17.2, 47.75) * mm});
            skLineSegment(sketch, "E18.40.2", {"start": v(-11.79, 40.57) * mm, "end": v(-14.16, 48.74) * mm});
            skArc(sketch, "E18.40.3", {"start": v(-10.5, 40.92) * mm, "mid": v(-12.42, 40.38) * mm, "end": v(-14.31, 39.75) * mm});
            skLineSegment(sketch, "E18.40.4", {"start": v(-8.4, 32.7) * mm, "end": v(-10.5, 40.92) * mm});
            skArc(sketch, "E18.40.5", {"start": v(-8.4, 32.7) * mm, "mid": v(-9.42, 32.41) * mm, "end": v(-10.43, 32.1) * mm});
            skLineSegment(sketch, "E18.40.6", {"start": v(-10.43, 32.1) * mm, "end": v(-13.06, 40.18) * mm});
            skLineSegment(sketch, "E18.41.0", {"start": v(-19.18, 37.65) * mm, "end": v(-23.04, 45.22) * mm});
            skArc(sketch, "E18.41.1", {"start": v(-20.16, 46.58) * mm, "mid": v(-21.6, 45.92) * mm, "end": v(-23.04, 45.22) * mm});
            skLineSegment(sketch, "E18.41.2", {"start": v(-16.78, 38.78) * mm, "end": v(-20.16, 46.58) * mm});
            skArc(sketch, "E18.41.3", {"start": v(-15.55, 39.28) * mm, "mid": v(-17.39, 38.5) * mm, "end": v(-19.18, 37.65) * mm});
            skLineSegment(sketch, "E18.41.4", {"start": v(-12.42, 31.38) * mm, "end": v(-15.55, 39.28) * mm});
            skArc(sketch, "E18.41.5", {"start": v(-12.42, 31.38) * mm, "mid": v(-13.4, 30.98) * mm, "end": v(-14.37, 30.54) * mm});
            skLineSegment(sketch, "E18.41.6", {"start": v(-14.37, 30.54) * mm, "end": v(-17.99, 38.23) * mm});
            skLineSegment(sketch, "E18.42.0", {"start": v(-23.75, 34.94) * mm, "end": v(-28.53, 41.98) * mm});
            skArc(sketch, "E18.42.1", {"start": v(-25.83, 43.68) * mm, "mid": v(-27.2, 42.85) * mm, "end": v(-28.53, 41.98) * mm});
            skLineSegment(sketch, "E18.42.2", {"start": v(-21.5, 36.37) * mm, "end": v(-25.83, 43.68) * mm});
            skArc(sketch, "E18.42.3", {"start": v(-20.35, 37.02) * mm, "mid": v(-22.08, 36.02) * mm, "end": v(-23.75, 34.94) * mm});
            skLineSegment(sketch, "E18.42.4", {"start": v(-16.26, 29.58) * mm, "end": v(-20.35, 37.02) * mm});
            skArc(sketch, "E18.42.5", {"start": v(-16.26, 29.58) * mm, "mid": v(-17.18, 29.05) * mm, "end": v(-18.08, 28.5) * mm});
            skLineSegment(sketch, "E18.42.6", {"start": v(-18.08, 28.5) * mm, "end": v(-22.64, 35.67) * mm});
            skLineSegment(sketch, "E18.43.0", {"start": v(-27.94, 31.7) * mm, "end": v(-33.56, 38.07) * mm});
            skArc(sketch, "E18.43.1", {"start": v(-31.1, 40.1) * mm, "mid": v(-32.35, 39.1) * mm, "end": v(-33.56, 38.07) * mm});
            skLineSegment(sketch, "E18.43.2", {"start": v(-25.9, 33.38) * mm, "end": v(-31.1, 40.1) * mm});
            skArc(sketch, "E18.43.3", {"start": v(-24.83, 34.18) * mm, "mid": v(-26.42, 32.97) * mm, "end": v(-27.94, 31.7) * mm});
            skLineSegment(sketch, "E18.43.4", {"start": v(-19.84, 27.3) * mm, "end": v(-24.83, 34.18) * mm});
            skArc(sketch, "E18.43.5", {"start": v(-19.84, 27.3) * mm, "mid": v(-20.69, 26.67) * mm, "end": v(-21.51, 26) * mm});
            skLineSegment(sketch, "E18.43.6", {"start": v(-21.51, 26) * mm, "end": v(-26.93, 32.55) * mm});
            skLineSegment(sketch, "E18.44.0", {"start": v(-31.7, 27.94) * mm, "end": v(-38.07, 33.56) * mm});
            skArc(sketch, "E18.44.1", {"start": v(-35.89, 35.89) * mm, "mid": v(-37, 34.74) * mm, "end": v(-38.07, 33.56) * mm});
            skLineSegment(sketch, "E18.44.2", {"start": v(-29.88, 29.88) * mm, "end": v(-35.89, 35.89) * mm});
            skArc(sketch, "E18.44.3", {"start": v(-28.92, 30.8) * mm, "mid": v(-30.34, 29.4) * mm, "end": v(-31.7, 27.94) * mm});
            skLineSegment(sketch, "E18.44.4", {"start": v(-23.1, 24.6) * mm, "end": v(-28.92, 30.8) * mm});
            skArc(sketch, "E18.44.5", {"start": v(-23.1, 24.6) * mm, "mid": v(-23.87, 23.87) * mm, "end": v(-24.6, 23.1) * mm});
            skLineSegment(sketch, "E18.44.6", {"start": v(-24.6, 23.1) * mm, "end": v(-30.8, 28.92) * mm});
            skLineSegment(sketch, "E18.45.0", {"start": v(-34.94, 23.75) * mm, "end": v(-41.98, 28.53) * mm});
            skArc(sketch, "E18.45.1", {"start": v(-40.1, 31.1) * mm, "mid": v(-41.06, 29.83) * mm, "end": v(-41.98, 28.53) * mm});
            skLineSegment(sketch, "E18.45.2", {"start": v(-33.38, 25.9) * mm, "end": v(-40.1, 31.1) * mm});
            skArc(sketch, "E18.45.3", {"start": v(-32.55, 26.93) * mm, "mid": v(-33.79, 25.37) * mm, "end": v(-34.94, 23.75) * mm});
            skLineSegment(sketch, "E18.45.4", {"start": v(-26, 21.51) * mm, "end": v(-32.55, 26.93) * mm});
            skArc(sketch, "E18.45.5", {"start": v(-26, 21.51) * mm, "mid": v(-26.67, 20.69) * mm, "end": v(-27.3, 19.84) * mm});
            skLineSegment(sketch, "E18.45.6", {"start": v(-27.3, 19.84) * mm, "end": v(-34.18, 24.83) * mm});
            skLineSegment(sketch, "E18.46.0", {"start": v(-37.65, 19.18) * mm, "end": v(-45.22, 23.04) * mm});
            skArc(sketch, "E18.46.1", {"start": v(-43.68, 25.83) * mm, "mid": v(-44.47, 24.45) * mm, "end": v(-45.22, 23.04) * mm});
            skLineSegment(sketch, "E18.46.2", {"start": v(-36.37, 21.5) * mm, "end": v(-43.68, 25.83) * mm});
            skArc(sketch, "E18.46.3", {"start": v(-35.67, 22.64) * mm, "mid": v(-36.7, 20.93) * mm, "end": v(-37.65, 19.18) * mm});
            skLineSegment(sketch, "E18.46.4", {"start": v(-28.5, 18.08) * mm, "end": v(-35.67, 22.64) * mm});
            skArc(sketch, "E18.46.5", {"start": v(-28.5, 18.08) * mm, "mid": v(-29.05, 17.18) * mm, "end": v(-29.58, 16.26) * mm});
            skLineSegment(sketch, "E18.46.6", {"start": v(-29.58, 16.26) * mm, "end": v(-37.02, 20.35) * mm});
            skLineSegment(sketch, "E18.47.0", {"start": v(-39.75, 14.31) * mm, "end": v(-47.75, 17.2) * mm});
            skArc(sketch, "E18.47.1", {"start": v(-46.58, 20.16) * mm, "mid": v(-47.19, 18.68) * mm, "end": v(-47.75, 17.2) * mm});
            skLineSegment(sketch, "E18.47.2", {"start": v(-38.78, 16.78) * mm, "end": v(-46.58, 20.16) * mm});
            skArc(sketch, "E18.47.3", {"start": v(-38.23, 17.99) * mm, "mid": v(-39.03, 16.17) * mm, "end": v(-39.75, 14.31) * mm});
            skLineSegment(sketch, "E18.47.4", {"start": v(-30.54, 14.37) * mm, "end": v(-38.23, 17.99) * mm});
            skArc(sketch, "E18.47.5", {"start": v(-30.54, 14.37) * mm, "mid": v(-30.98, 13.4) * mm, "end": v(-31.38, 12.42) * mm});
            skLineSegment(sketch, "E18.47.6", {"start": v(-31.38, 12.42) * mm, "end": v(-39.28, 15.55) * mm});
            skLineSegment(sketch, "E18.48.0", {"start": v(-41.23, 9.22) * mm, "end": v(-49.53, 11.07) * mm});
            skArc(sketch, "E18.48.1", {"start": v(-48.74, 14.16) * mm, "mid": v(-49.16, 12.62) * mm, "end": v(-49.53, 11.07) * mm});
            skLineSegment(sketch, "E18.48.2", {"start": v(-40.57, 11.79) * mm, "end": v(-48.74, 14.16) * mm});
            skArc(sketch, "E18.48.3", {"start": v(-40.18, 13.06) * mm, "mid": v(-40.75, 11.15) * mm, "end": v(-41.23, 9.22) * mm});
            skLineSegment(sketch, "E18.48.4", {"start": v(-32.1, 10.43) * mm, "end": v(-40.18, 13.06) * mm});
            skArc(sketch, "E18.48.5", {"start": v(-32.1, 10.43) * mm, "mid": v(-32.41, 9.42) * mm, "end": v(-32.7, 8.4) * mm});
            skLineSegment(sketch, "E18.48.6", {"start": v(-32.7, 8.4) * mm, "end": v(-40.92, 10.5) * mm});
            skLineSegment(sketch, "E18.49.0", {"start": v(-42.06, 3.98) * mm, "end": v(-50.53, 4.78) * mm});
            skArc(sketch, "E18.49.1", {"start": v(-50.13, 7.94) * mm, "mid": v(-50.35, 6.36) * mm, "end": v(-50.53, 4.78) * mm});
            skLineSegment(sketch, "E18.49.2", {"start": v(-41.73, 6.6) * mm, "end": v(-50.13, 7.94) * mm});
            skArc(sketch, "E18.49.3", {"start": v(-41.5, 7.92) * mm, "mid": v(-41.83, 5.95) * mm, "end": v(-42.06, 3.98) * mm});
            skLineSegment(sketch, "E18.49.4", {"start": v(-33.15, 6.32) * mm, "end": v(-41.5, 7.92) * mm});
            skArc(sketch, "E18.49.5", {"start": v(-33.15, 6.32) * mm, "mid": v(-33.34, 5.28) * mm, "end": v(-33.48, 4.23) * mm});
            skLineSegment(sketch, "E18.49.6", {"start": v(-33.48, 4.23) * mm, "end": v(-41.92, 5.3) * mm});
            skCircle(sketch, "E19", {"center": v(0, 0) * mm, "radius": 13.33 * mm});
            skSolve(sketch);
        }
        {
            var Q0;
            Q0 = qSketchRegion(id + "F0", true);
            extrude(context, id + "F1", {"entities" : qUnion([Q0]), "depth" : .1 * mm, "offsetDistance" : 25 * mm});
        }
    });
